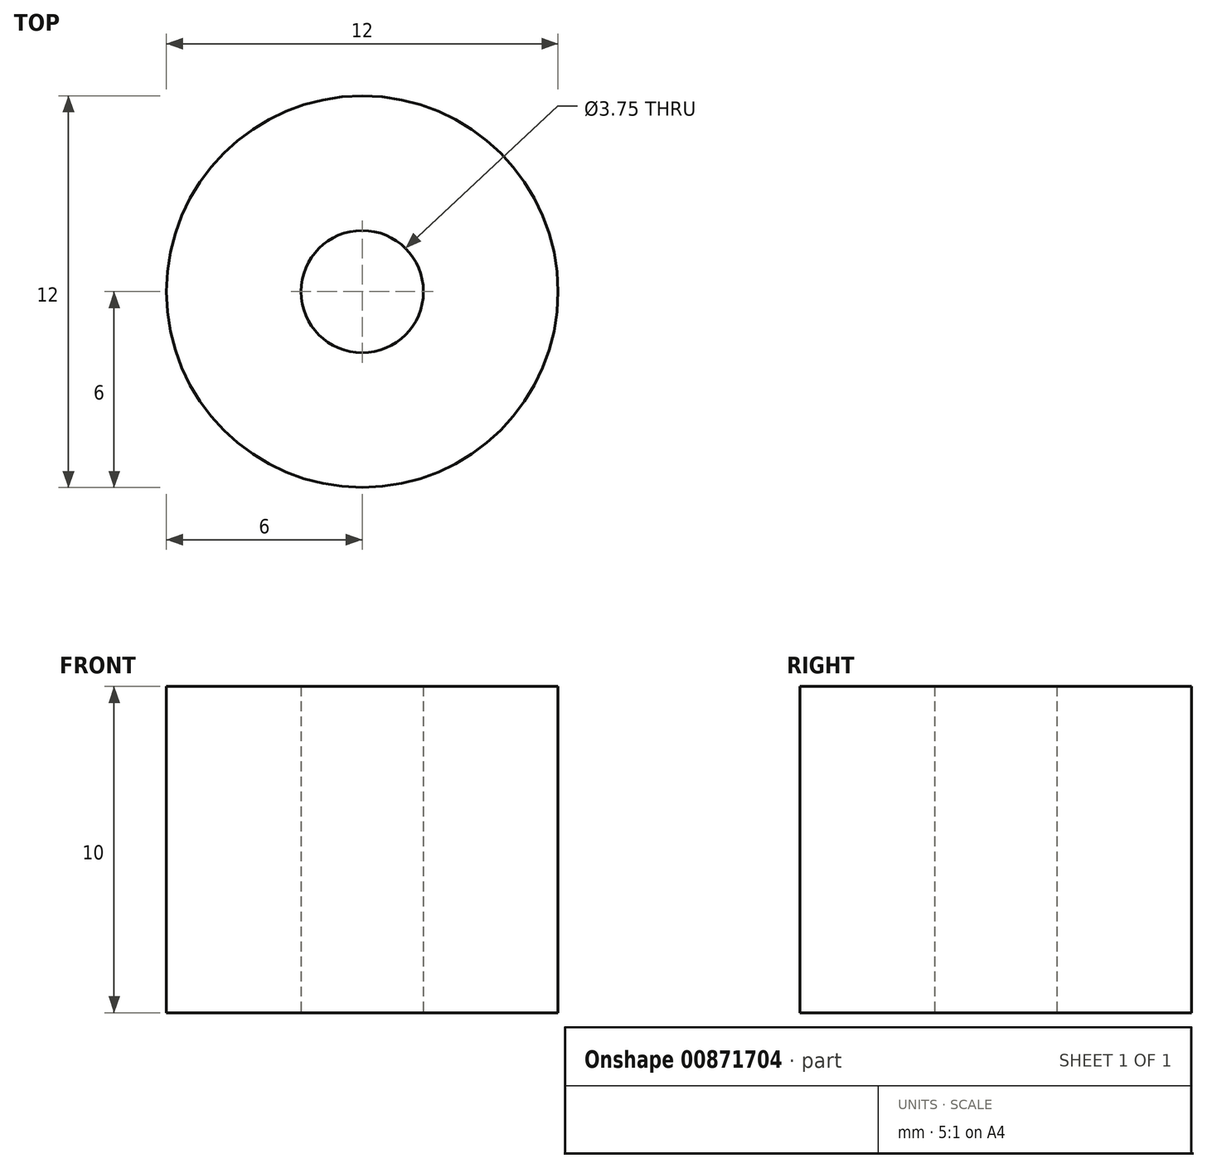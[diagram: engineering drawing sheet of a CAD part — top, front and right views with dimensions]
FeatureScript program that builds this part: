
annotation { "Feature Type Name" : "Feature", "Feature Type Description" : "" }
export const myFeature = defineFeature(function(context is Context, id is Id, definition is map)
    precondition{}
    {
        {
            var Q0;
            Q0=qCreatedBy(makeId("Top.planeOp"),FACE);
            var sketch = newSketch(context, id + "F0", { "sketchPlane" : qUnion([Q0])});
            skCircle(sketch, "E0", {"center": v(0, 0) * mm, "radius": 6 * mm});
            skCircle(sketch, "E1", {"center": v(0, 0) * mm, "radius": 1.88 * mm});
            skSolve(sketch);
        }
        {
            var Q0;
            Q0=makeQuery(id+"F0.imprint","IMPRINT",FACE,{"disambiguationData":[TD([[makeQuery(id+"F0.imprint","IMPRINT",EDGE,{"derivedFrom":sQuery(id+"F0.wireOp",EDGE,"E0")}),1.0]])]});
            extrude(context, id + "F1", {"entities" : qUnion([Q0]), "depth" : 10 * mm, "offsetDistance" : 25 * mm});
        }
    });
